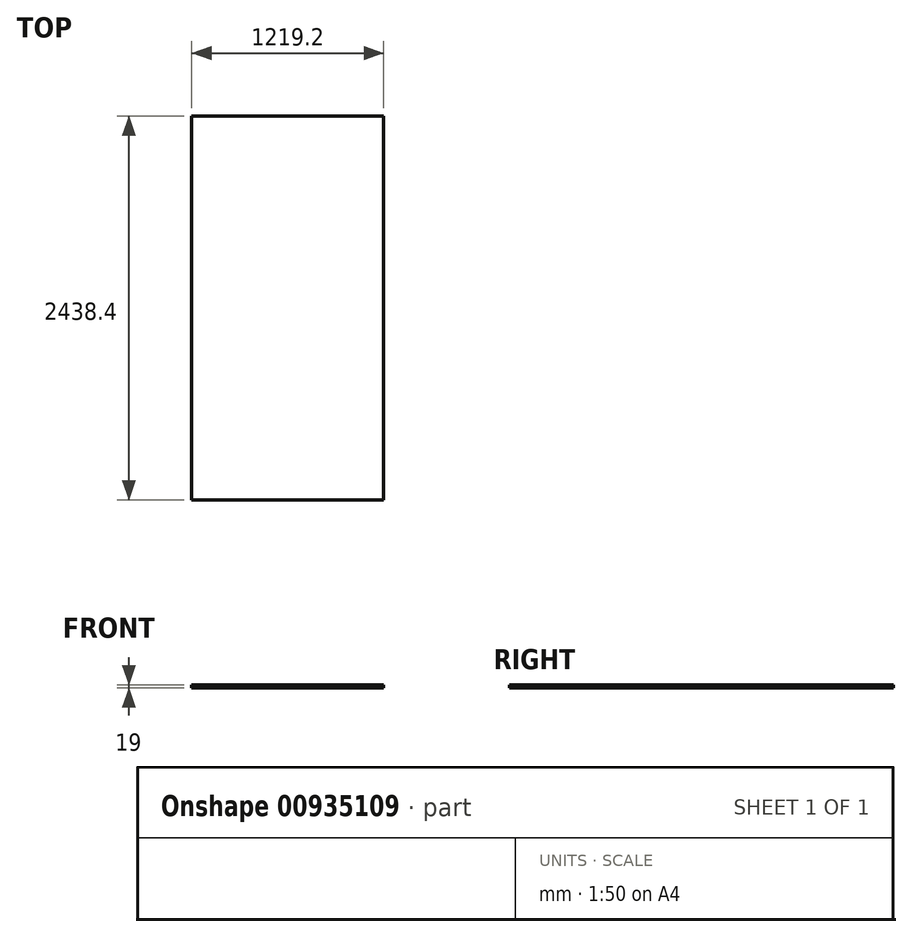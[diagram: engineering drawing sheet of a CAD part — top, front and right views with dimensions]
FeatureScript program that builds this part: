
annotation { "Feature Type Name" : "Feature", "Feature Type Description" : "" }
export const myFeature = defineFeature(function(context is Context, id is Id, definition is map)
    precondition{}
    {
        {
            var Q0;
            Q0=qCreatedBy(makeId("Top.planeOp"),FACE);
            var sketch = newSketch(context, id + "F0", { "sketchPlane" : qUnion([Q0])});
            skLineSegment(sketch, "E0.bottom", {"start": v(0, 0) * mm, "end": v(1219.2, 0) * mm});
            skLineSegment(sketch, "E0.top", {"start": v(0, 2438.4) * mm, "end": v(1219.2, 2438.4) * mm});
            skLineSegment(sketch, "E0.left", {"start": v(0, 0) * mm, "end": v(0, 2438.4) * mm});
            skLineSegment(sketch, "E0.right", {"start": v(1219.2, 0) * mm, "end": v(1219.2, 2438.4) * mm});
            skSolve(sketch);
        }
        {
            var Q0;
            Q0 = qSketchRegion(id + "F0", true);
            extrude(context, id + "F1", {"entities" : qUnion([Q0]), "oppositeDirection" : true, "depth" : 19 * mm, "offsetDistance" : 25 * mm});
        }
    });
